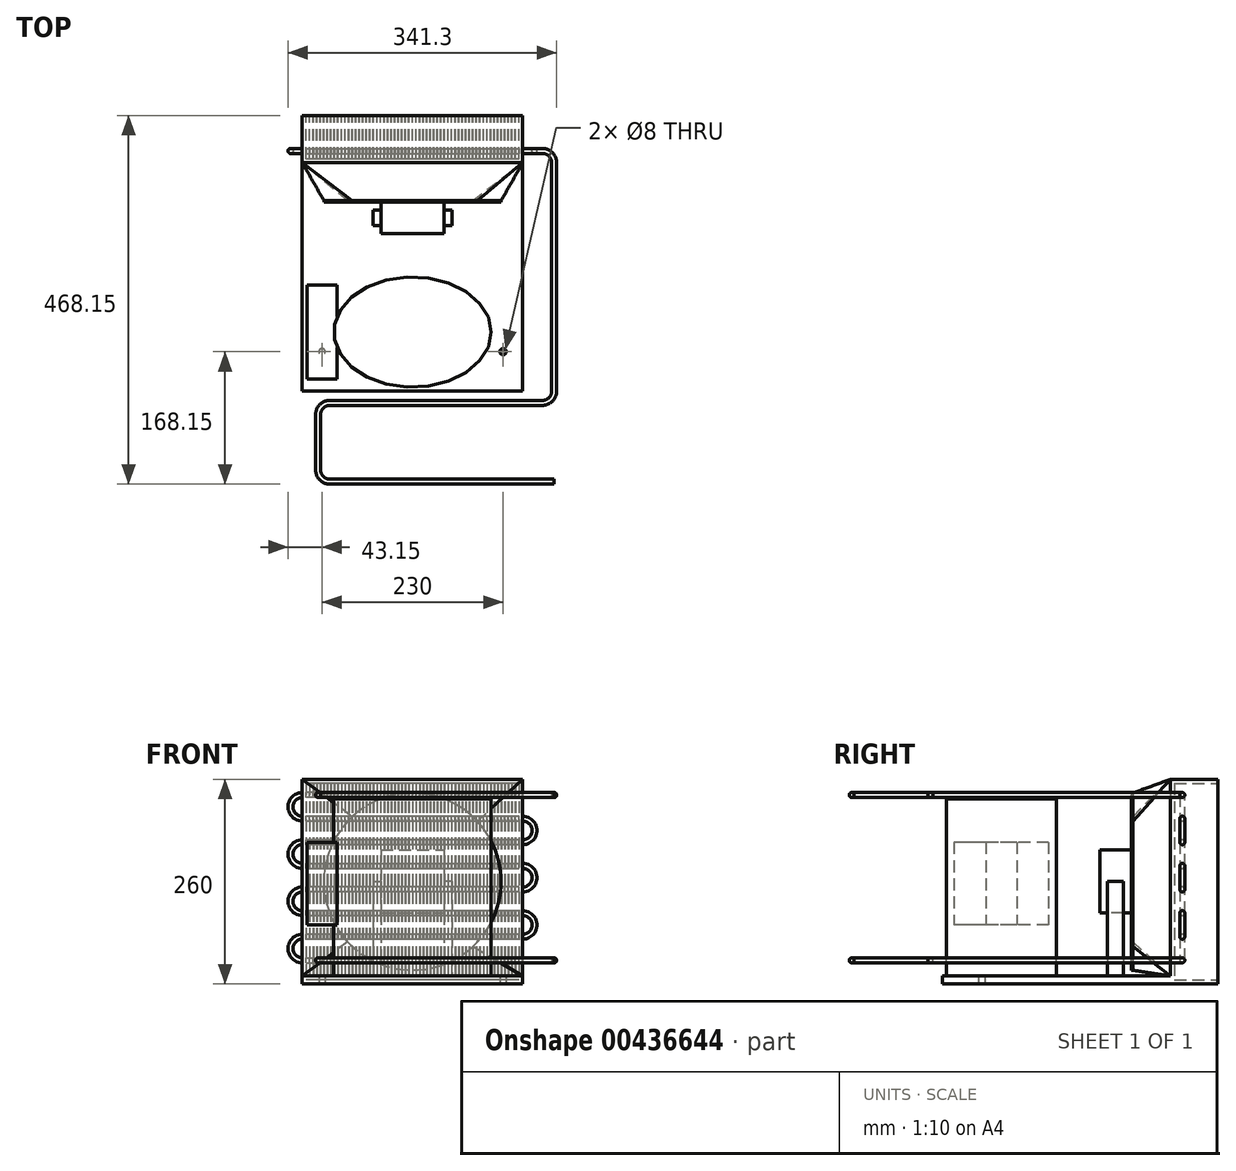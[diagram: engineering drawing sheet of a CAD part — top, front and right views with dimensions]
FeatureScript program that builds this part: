
annotation { "Feature Type Name" : "Feature", "Feature Type Description" : "" }
export const myFeature = defineFeature(function(context is Context, id is Id, definition is map)
    precondition{}
    {
        {
            var Q0;
            Q0=qCreatedBy(makeId("Top.planeOp"),FACE);
            var sketch = newSketch(context, id + "F0", { "sketchPlane" : qUnion([Q0])});
            skLineSegment(sketch, "E0", {"start": v(0, 0) * mm, "end": v(280, 0) * mm});
            skLineSegment(sketch, "E1", {"start": v(280, -350) * mm, "end": v(0, -350) * mm});
            skLineSegment(sketch, "E2", {"start": v(0, -350) * mm, "end": v(0, 0) * mm});
            skLineSegment(sketch, "E3", {"start": v(280, 0) * mm, "end": v(280, -60) * mm});
            skLineSegment(sketch, "E4", {"start": v(280, -60) * mm, "end": v(0, -60) * mm});
            skLineSegment(sketch, "E5", {"start": v(280, -350) * mm, "end": v(280, -200) * mm});
            skLineSegment(sketch, "E6", {"start": v(280, -200) * mm, "end": v(280, -60) * mm});
            skLineSegment(sketch, "E7", {"start": v(280, -275) * mm, "end": v(140, -275) * mm, "construction": true});
            skPoint(sketch, "E7.endSnap0", {"position": v(280, -275) * mm});
            skEllipse(sketch, "E8", {"center": v(140, -275) * mm, "majorRadius": 100 * mm, "minorRadius": 70 * mm, "majorAxis": v(1, 0)});
            skPoint(sketch, "E9.endSnap0", {"position": v(40, -275) * mm});
            skLineSegment(sketch, "E10.bottom", {"start": v(44, -215) * mm, "end": v(6, -215) * mm});
            skLineSegment(sketch, "E10.top", {"start": v(44, -335) * mm, "end": v(6, -335) * mm});
            skLineSegment(sketch, "E10.left", {"start": v(44, -215) * mm, "end": v(44, -335) * mm});
            skLineSegment(sketch, "E10.right", {"start": v(6, -215) * mm, "end": v(6, -335) * mm});
            skLineSegment(sketch, "E11", {"start": v(140, -60) * mm, "end": v(140, -110) * mm, "construction": true});
            skLineSegment(sketch, "E12", {"start": v(140, -110) * mm, "end": v(100, -110) * mm, "construction": true});
            skLineSegment(sketch, "E13.bottom", {"start": v(100, -110) * mm, "end": v(180, -110) * mm});
            skLineSegment(sketch, "E13.top", {"start": v(100, -150) * mm, "end": v(180, -150) * mm});
            skLineSegment(sketch, "E13.right", {"start": v(180, -110) * mm, "end": v(180, -150) * mm});
            skLineSegment(sketch, "E14.top", {"start": v(90, -140) * mm, "end": v(100, -140) * mm});
            skLineSegment(sketch, "E15.top", {"start": v(90, -120) * mm, "end": v(100, -120) * mm});
            skLineSegment(sketch, "E16", {"start": v(90, -120) * mm, "end": v(90, -140) * mm});
            skLineSegment(sketch, "E17", {"start": v(100, -150) * mm, "end": v(100, -110) * mm});
            skLineSegment(sketch, "E18", {"start": v(180, -140) * mm, "end": v(190, -140) * mm});
            skLineSegment(sketch, "E19", {"start": v(190, -140) * mm, "end": v(190, -120) * mm});
            skLineSegment(sketch, "E20", {"start": v(190, -120) * mm, "end": v(180, -120) * mm});
            skLineSegment(sketch, "E21", {"start": v(140, -275) * mm, "end": v(6, -275) * mm, "construction": true});
            skLineSegment(sketch, "E22", {"start": v(280, -350) * mm, "end": v(280, -300) * mm});
            skLineSegment(sketch, "E23", {"start": v(280, -300) * mm, "end": v(255, -300) * mm, "construction": true});
            skCircle(sketch, "E24", {"center": v(255, -300) * mm, "radius": 4 * mm});
            skLineSegment(sketch, "E25", {"start": v(255, -300) * mm, "end": v(25, -300) * mm, "construction": true});
            skCircle(sketch, "E26", {"center": v(25, -300) * mm, "radius": 4 * mm});
            skSolve(sketch);
        }
        {
            var Q0;
            {var subQ5=sQuery(id+"F0.wireOp",EDGE,"E1");Q0=makeQuery(id+"F0.imprint","IMPRINT",FACE,{"disambiguationData":[TD([[makeQuery(id+"F0.imprint","IMPRINT",EDGE,{"derivedFrom":subQ5}),-1.0]])]});}
            var Q1;
            Q1=makeQuery(id+"F0.imprint","IMPRINT",FACE,{"disambiguationData":[TD([[makeQuery(id+"F0.imprint","IMPRINT",EDGE,{"derivedFrom":sQuery(id+"F0.wireOp",EDGE,"E10.bottom")}),1.0]])]});
            var Q2;
            {var subQ3=sQuery(id+"F0.wireOp",EDGE,"E13.bottom");Q2=makeQuery(id+"F0.imprint","IMPRINT",FACE,{"disambiguationData":[TD([[makeQuery(id+"F0.imprint","IMPRINT",EDGE,{"derivedFrom":subQ3}),-1.0]])]});}
            extrude(context, id + "F1", {"entities" : qUnion([Q0, Q1, Q2]), "depth" : 10 * mm});
        }
        {
            var Q0;
            {var subQ0=sQuery(id+"F0.wireOp",EDGE,"E0");Q0=makeQuery(id+"F0.imprint","IMPRINT",FACE,{"disambiguationData":[TD([[makeQuery(id+"F0.imprint","IMPRINT",EDGE,{"derivedFrom":subQ0}),-1.0]])]});}
            extrude(context, id + "F2", {"entities" : qUnion([Q0]), "operationType" : NewBodyOperationType.ADD, "depth" : 260 * mm});
        }
        {
            var Q0;
            Q0=makeQuery(id+"F0.imprint","IMPRINT",FACE,{"disambiguationData":[TD([[makeQuery(id+"F0.imprint","IMPRINT",EDGE,{"derivedFrom":sQuery(id+"F0.wireOp",EDGE,"E8")}),1.0]])]});
            extrude(context, id + "F3", {"entities" : qUnion([Q0]), "operationType" : NewBodyOperationType.ADD, "depth" : 235 * mm});
        }
        {
            var Q0;
            Q0=makeQuery(id+"F0.imprint","IMPRINT",FACE,{"disambiguationData":[TD([[makeQuery(id+"F0.imprint","IMPRINT",EDGE,{"derivedFrom":sQuery(id+"F0.wireOp",EDGE,"E10.bottom")}),1.0]])]});
            var Q1;
            Q1=makeQuery(id+"F0.imprint","IMPRINT",FACE,{"disambiguationData":[TD([[makeQuery(id+"F0.imprint","IMPRINT",EDGE,{"derivedFrom":sQuery(id+"F0.wireOp",EDGE,"E26")}),1.0]])]});
            extrude(context, id + "F4", {"entities" : qUnion([Q0, Q1]), "operationType" : NewBodyOperationType.ADD, "depth" : 180 * mm, "hasSecondDirection" : true, "secondDirectionOppositeDirection" : false, "secondDirectionDepth" : 75 * mm});
        }
        {
            var Q0;
            {var subQ0=sQuery(id+"F0.wireOp",EDGE,"E14.top");Q0=makeQuery(id+"F0.imprint","IMPRINT",FACE,{"disambiguationData":[TD([[makeQuery(id+"F0.imprint","IMPRINT",EDGE,{"derivedFrom":subQ0}),1.0]])]});}
            var Q1;
            {var subQ0=sQuery(id+"F0.wireOp",EDGE,"E18");Q1=makeQuery(id+"F0.imprint","IMPRINT",FACE,{"disambiguationData":[TD([[makeQuery(id+"F0.imprint","IMPRINT",EDGE,{"derivedFrom":subQ0}),1.0]])]});}
            extrude(context, id + "F5", {"entities" : qUnion([Q0, Q1]), "operationType" : NewBodyOperationType.ADD, "depth" : 130 * mm});
        }
        {
            var Q0;
            {var subQ3=sQuery(id+"F0.wireOp",EDGE,"E13.bottom");Q0=makeQuery(id+"F0.imprint","IMPRINT",FACE,{"disambiguationData":[TD([[makeQuery(id+"F0.imprint","IMPRINT",EDGE,{"derivedFrom":subQ3}),-1.0]])]});}
            extrude(context, id + "F6", {"entities" : qUnion([Q0]), "operationType" : NewBodyOperationType.ADD, "depth" : 170 * mm, "hasSecondDirection" : true, "secondDirectionOppositeDirection" : false, "secondDirectionDepth" : 90 * mm});
        }
        {
            var Q0;
            Q0=makeQuery(id+"F6.opExtrude","SWEPT_FACE",FACE,{"disambiguationData":[OSD([sQuery(id+"F0.wireOp",EDGE,"E13.bottom")])]});
            var sketch = newSketch(context, id + "F7", { "sketchPlane" : qUnion([Q0])});
            skLineSegment(sketch, "E27", {"start": v(-140, 170) * mm, "end": v(-140, 90) * mm, "construction": true});
            skCircle(sketch, "E28", {"center": v(-140, 130) * mm, "radius": 112.5 * mm});
            skSolve(sketch);
        }
        {
            var Q0;
            Q0=makeQuery(id+"F7.imprint","IMPRINT",FACE,{"disambiguationData":[TD([[makeQuery(id+"F7.imprint","IMPRINT",EDGE,{"derivedFrom":sQuery(id+"F7.wireOp",EDGE,"E28")}),1.0]])]});
            var Q1;
            {var subQ0=sQuery(id+"F0.wireOp",EDGE,"E13.bottom");Q1=makeQuery(id+"F7.imprint","IMPRINT",FACE,{"disambiguationData":[TD([[makeQuery(id+"F7.imprint","IMPRINT",EDGE,{"derivedFrom":makeQuery(id+"F6.opExtrude","CAP_EDGE",EDGE,{"disambiguationData":[OSD([subQ0])],"isStart":true})}),-1.0]])]});}
            extrude(context, id + "F8", {"entities" : qUnion([Q0, Q1]), "operationType" : NewBodyOperationType.ADD, "depth" : 2 * mm});
        }
        {
            var Q1;
            Q1=makeQuery(id+"F8.opExtrude","CAP_FACE",FACE,{"disambiguationData":[OSD([sQuery(id+"F7.wireOp",EDGE,"E28")])],"isStart":false});
            var Q2;
            Q2=makeQuery(id+"F2.opExtrude","SWEPT_FACE",FACE,{"disambiguationData":[OSD([sQuery(id+"F0.wireOp",EDGE,"E4")])]});
            loft(context, id + "F9", {"operationType" : NewBodyOperationType.ADD, "sheetProfilesArray" : [{ "sheetProfileEntities" : qUnion([Q1]) }, { "sheetProfileEntities" : qUnion([Q2]) }]});
        }
        {
            var Q0;
            Q0=makeQuery(id+"F2.boolean.opBoolean","MERGE",FACE,{"derivedFrom":[makeQuery(id+"F1.opExtrude","SWEPT_FACE",FACE,{"disambiguationData":[OSD([sQuery(id+"F0.wireOp",EDGE,"E5"),sQuery(id+"F0.wireOp",EDGE,"E6")])]}),makeQuery(id+"F2.opExtrude","SWEPT_FACE",FACE,{"disambiguationData":[OSD([sQuery(id+"F0.wireOp",EDGE,"E3")])]})]});
            var sketch = newSketch(context, id + "F10", { "sketchPlane" : qUnion([Q0])});
            skLineSegment(sketch, "E29", {"start": v(-30, 260) * mm, "end": v(-30, 240) * mm, "construction": true});
            skLineSegment(sketch, "E30", {"start": v(-30, 240) * mm, "end": v(-45, 240) * mm, "construction": true});
            skCircle(sketch, "E31", {"center": v(-45, 240) * mm, "radius": 3.15 * mm});
            skLineSegment(sketch, "E32", {"start": v(-45, 240) * mm, "end": v(-45, 30) * mm, "construction": true});
            skCircle(sketch, "E33", {"center": v(-45, 30) * mm, "radius": 3.15 * mm});
            skSolve(sketch);
        }
        {
            var Q0;
            Q0=makeQuery(id+"F2.opExtrude","CAP_FACE",FACE,{"disambiguationData":[OSD([sQuery(id+"F0.wireOp",EDGE,"E0"),sQuery(id+"F0.wireOp",EDGE,"E2"),sQuery(id+"F0.wireOp",EDGE,"E3"),sQuery(id+"F0.wireOp",EDGE,"E4")])],"isStart":false});
            var sketch = newSketch(context, id + "F11", { "sketchPlane" : qUnion([Q0])});
            skLineSegment(sketch, "E34", {"start": v(280, -30) * mm, "end": v(280, -45) * mm, "construction": true});
            skLineSegment(sketch, "E35", {"start": v(280, -45) * mm, "end": v(305, -45) * mm});
            skLineSegment(sketch, "E36", {"start": v(320, -60) * mm, "end": v(320, -350) * mm});
            skPoint(sketch, "E37.visualSharp", {"position": v(320, -45) * mm});
            skArc(sketch, "E37.filletArc", {"start": v(320, -60) * mm, "mid": v(315.6, -49.4) * mm, "end": v(305, -45) * mm});
            skLineSegment(sketch, "E38", {"start": v(305, -365) * mm, "end": v(35, -365) * mm});
            skPoint(sketch, "E39.visualSharp", {"position": v(320, -365) * mm});
            skArc(sketch, "E39.filletArc", {"start": v(305, -365) * mm, "mid": v(315.6, -360.6) * mm, "end": v(320, -350) * mm});
            skLineSegment(sketch, "E40", {"start": v(20, -380) * mm, "end": v(20, -450) * mm});
            skLineSegment(sketch, "E41", {"start": v(35, -465) * mm, "end": v(320, -465) * mm});
            skPoint(sketch, "E42.visualSharp", {"position": v(20, -365) * mm});
            skArc(sketch, "E42.filletArc", {"start": v(35, -365) * mm, "mid": v(24.4, -369.4) * mm, "end": v(20, -380) * mm});
            skPoint(sketch, "E43.visualSharp", {"position": v(20, -465) * mm});
            skArc(sketch, "E43.filletArc", {"start": v(20, -450) * mm, "mid": v(24.4, -460.6) * mm, "end": v(35, -465) * mm});
            skSolve(sketch);
        }
        {
            var Q0;
            Q0=makeQuery(id+"F10.imprint","IMPRINT",FACE,{"disambiguationData":[TD([[makeQuery(id+"F10.imprint","IMPRINT",EDGE,{"derivedFrom":sQuery(id+"F10.wireOp",EDGE,"E31")}),1.0]])]});
            var Q1;
            Q1=makeQuery(id+"F10.imprint","IMPRINT",FACE,{"disambiguationData":[TD([[makeQuery(id+"F10.imprint","IMPRINT",EDGE,{"derivedFrom":sQuery(id+"F10.wireOp",EDGE,"E33")}),1.0]])]});
            var Q2;
            Q2=sQuery(id+"F11.wireOp",EDGE,"E35");
            var Q3;
            Q3=sQuery(id+"F11.wireOp",EDGE,"E37.filletArc");
            var Q4;
            Q4=sQuery(id+"F11.wireOp",EDGE,"E36");
            var Q5;
            Q5=sQuery(id+"F11.wireOp",EDGE,"E39.filletArc");
            var Q6;
            Q6=sQuery(id+"F11.wireOp",EDGE,"E38");
            var Q7;
            Q7=sQuery(id+"F11.wireOp",EDGE,"E42.filletArc");
            var Q8;
            Q8=sQuery(id+"F11.wireOp",EDGE,"E40");
            var Q9;
            Q9=sQuery(id+"F11.wireOp",EDGE,"E43.filletArc");
            var Q10;
            Q10=sQuery(id+"F11.wireOp",EDGE,"E41");
            sweep(context, id + "F12", {"operationType" : NewBodyOperationType.ADD, "profiles" : qUnion([Q0, Q1]), "path" : qUnion([Q2, Q3, Q4, Q5, Q6, Q7, Q8, Q9, Q10])});
        }
        {
            var Q0;
            Q0=makeQuery(id+"F2.opExtrude","SWEPT_FACE",FACE,{"disambiguationData":[OSD([sQuery(id+"F0.wireOp",EDGE,"E0")])]});
            var sketch = newSketch(context, id + "F13", { "sketchPlane" : qUnion([Q0])});
            skLineSegment(sketch, "E44", {"start": v(-280, 260) * mm, "end": v(-275, 260) * mm, "construction": true});
            skLineSegment(sketch, "E45", {"start": v(-275, 260) * mm, "end": v(-275, 255) * mm, "construction": true});
            skLineSegment(sketch, "E46.bottom", {"start": v(-275, 255) * mm, "end": v(-271, 255) * mm});
            skLineSegment(sketch, "E46.top", {"start": v(-275, 5) * mm, "end": v(-271, 5) * mm});
            skLineSegment(sketch, "E46.left", {"start": v(-275, 255) * mm, "end": v(-275, 5) * mm});
            skLineSegment(sketch, "E46.right", {"start": v(-271, 255) * mm, "end": v(-271, 5) * mm});
            skLineSegment(sketch, "E47.1.0.0", {"start": v(-266.5, 255) * mm, "end": v(-266.5, 5) * mm});
            skLineSegment(sketch, "E47.1.0.1", {"start": v(-270.5, 255) * mm, "end": v(-270.5, 5) * mm});
            skLineSegment(sketch, "E47.1.0.2", {"start": v(-270.5, 255) * mm, "end": v(-266.5, 255) * mm});
            skLineSegment(sketch, "E47.1.0.3", {"start": v(-270.5, 5) * mm, "end": v(-266.5, 5) * mm});
            skLineSegment(sketch, "E47.2.0.0", {"start": v(-261.98, 255) * mm, "end": v(-261.98, 5) * mm});
            skLineSegment(sketch, "E47.2.0.1", {"start": v(-265.98, 255) * mm, "end": v(-265.98, 5) * mm});
            skLineSegment(sketch, "E47.2.0.2", {"start": v(-265.98, 255) * mm, "end": v(-261.98, 255) * mm});
            skLineSegment(sketch, "E47.2.0.3", {"start": v(-265.98, 5) * mm, "end": v(-261.98, 5) * mm});
            skLineSegment(sketch, "E47.3.0.0", {"start": v(-257.47, 255) * mm, "end": v(-257.47, 5) * mm});
            skLineSegment(sketch, "E47.3.0.1", {"start": v(-261.47, 255) * mm, "end": v(-261.47, 5) * mm});
            skLineSegment(sketch, "E47.3.0.2", {"start": v(-261.47, 255) * mm, "end": v(-257.47, 255) * mm});
            skLineSegment(sketch, "E47.3.0.3", {"start": v(-261.47, 5) * mm, "end": v(-257.47, 5) * mm});
            skLineSegment(sketch, "E47.4.0.0", {"start": v(-252.97, 255) * mm, "end": v(-252.97, 5) * mm});
            skLineSegment(sketch, "E47.4.0.1", {"start": v(-256.97, 255) * mm, "end": v(-256.97, 5) * mm});
            skLineSegment(sketch, "E47.4.0.2", {"start": v(-256.97, 255) * mm, "end": v(-252.97, 255) * mm});
            skLineSegment(sketch, "E47.4.0.3", {"start": v(-256.97, 5) * mm, "end": v(-252.97, 5) * mm});
            skLineSegment(sketch, "E47.5.0.0", {"start": v(-248.46, 255) * mm, "end": v(-248.46, 5) * mm});
            skLineSegment(sketch, "E47.5.0.1", {"start": v(-252.46, 255) * mm, "end": v(-252.46, 5) * mm});
            skLineSegment(sketch, "E47.5.0.2", {"start": v(-252.46, 255) * mm, "end": v(-248.46, 255) * mm});
            skLineSegment(sketch, "E47.5.0.3", {"start": v(-252.46, 5) * mm, "end": v(-248.46, 5) * mm});
            skLineSegment(sketch, "E47.6.0.0", {"start": v(-243.95, 255) * mm, "end": v(-243.95, 5) * mm});
            skLineSegment(sketch, "E47.6.0.1", {"start": v(-247.95, 255) * mm, "end": v(-247.95, 5) * mm});
            skLineSegment(sketch, "E47.6.0.2", {"start": v(-247.95, 255) * mm, "end": v(-243.95, 255) * mm});
            skLineSegment(sketch, "E47.6.0.3", {"start": v(-247.95, 5) * mm, "end": v(-243.95, 5) * mm});
            skLineSegment(sketch, "E47.7.0.0", {"start": v(-239.44, 255) * mm, "end": v(-239.44, 5) * mm});
            skLineSegment(sketch, "E47.7.0.1", {"start": v(-243.44, 255) * mm, "end": v(-243.44, 5) * mm});
            skLineSegment(sketch, "E47.7.0.2", {"start": v(-243.44, 255) * mm, "end": v(-239.44, 255) * mm});
            skLineSegment(sketch, "E47.7.0.3", {"start": v(-243.44, 5) * mm, "end": v(-239.44, 5) * mm});
            skLineSegment(sketch, "E47.8.0.0", {"start": v(-234.93, 255) * mm, "end": v(-234.93, 5) * mm});
            skLineSegment(sketch, "E47.8.0.1", {"start": v(-238.93, 255) * mm, "end": v(-238.93, 5) * mm});
            skLineSegment(sketch, "E47.8.0.2", {"start": v(-238.93, 255) * mm, "end": v(-234.93, 255) * mm});
            skLineSegment(sketch, "E47.8.0.3", {"start": v(-238.93, 5) * mm, "end": v(-234.93, 5) * mm});
            skLineSegment(sketch, "E47.9.0.0", {"start": v(-230.42, 255) * mm, "end": v(-230.42, 5) * mm});
            skLineSegment(sketch, "E47.9.0.1", {"start": v(-234.42, 255) * mm, "end": v(-234.42, 5) * mm});
            skLineSegment(sketch, "E47.9.0.2", {"start": v(-234.42, 255) * mm, "end": v(-230.42, 255) * mm});
            skLineSegment(sketch, "E47.9.0.3", {"start": v(-234.42, 5) * mm, "end": v(-230.42, 5) * mm});
            skLineSegment(sketch, "E47.10.0.0", {"start": v(-225.92, 255) * mm, "end": v(-225.92, 5) * mm});
            skLineSegment(sketch, "E47.10.0.1", {"start": v(-229.92, 255) * mm, "end": v(-229.92, 5) * mm});
            skLineSegment(sketch, "E47.10.0.2", {"start": v(-229.92, 255) * mm, "end": v(-225.92, 255) * mm});
            skLineSegment(sketch, "E47.10.0.3", {"start": v(-229.92, 5) * mm, "end": v(-225.92, 5) * mm});
            skLineSegment(sketch, "E47.11.0.0", {"start": v(-221.4, 255) * mm, "end": v(-221.4, 5) * mm});
            skLineSegment(sketch, "E47.11.0.1", {"start": v(-225.4, 255) * mm, "end": v(-225.4, 5) * mm});
            skLineSegment(sketch, "E47.11.0.2", {"start": v(-225.4, 255) * mm, "end": v(-221.4, 255) * mm});
            skLineSegment(sketch, "E47.11.0.3", {"start": v(-225.4, 5) * mm, "end": v(-221.4, 5) * mm});
            skLineSegment(sketch, "E47.12.0.0", {"start": v(-216.9, 255) * mm, "end": v(-216.9, 5) * mm});
            skLineSegment(sketch, "E47.12.0.1", {"start": v(-220.9, 255) * mm, "end": v(-220.9, 5) * mm});
            skLineSegment(sketch, "E47.12.0.2", {"start": v(-220.9, 255) * mm, "end": v(-216.9, 255) * mm});
            skLineSegment(sketch, "E47.12.0.3", {"start": v(-220.9, 5) * mm, "end": v(-216.9, 5) * mm});
            skLineSegment(sketch, "E47.13.0.0", {"start": v(-212.39, 255) * mm, "end": v(-212.39, 5) * mm});
            skLineSegment(sketch, "E47.13.0.1", {"start": v(-216.39, 255) * mm, "end": v(-216.39, 5) * mm});
            skLineSegment(sketch, "E47.13.0.2", {"start": v(-216.39, 255) * mm, "end": v(-212.39, 255) * mm});
            skLineSegment(sketch, "E47.13.0.3", {"start": v(-216.39, 5) * mm, "end": v(-212.39, 5) * mm});
            skLineSegment(sketch, "E47.14.0.0", {"start": v(-207.88, 255) * mm, "end": v(-207.88, 5) * mm});
            skLineSegment(sketch, "E47.14.0.1", {"start": v(-211.88, 255) * mm, "end": v(-211.88, 5) * mm});
            skLineSegment(sketch, "E47.14.0.2", {"start": v(-211.88, 255) * mm, "end": v(-207.88, 255) * mm});
            skLineSegment(sketch, "E47.14.0.3", {"start": v(-211.88, 5) * mm, "end": v(-207.88, 5) * mm});
            skLineSegment(sketch, "E47.15.0.0", {"start": v(-203.37, 255) * mm, "end": v(-203.37, 5) * mm});
            skLineSegment(sketch, "E47.15.0.1", {"start": v(-207.37, 255) * mm, "end": v(-207.37, 5) * mm});
            skLineSegment(sketch, "E47.15.0.2", {"start": v(-207.37, 255) * mm, "end": v(-203.37, 255) * mm});
            skLineSegment(sketch, "E47.15.0.3", {"start": v(-207.37, 5) * mm, "end": v(-203.37, 5) * mm});
            skLineSegment(sketch, "E47.16.0.0", {"start": v(-198.86, 255) * mm, "end": v(-198.86, 5) * mm});
            skLineSegment(sketch, "E47.16.0.1", {"start": v(-202.86, 255) * mm, "end": v(-202.86, 5) * mm});
            skLineSegment(sketch, "E47.16.0.2", {"start": v(-202.86, 255) * mm, "end": v(-198.86, 255) * mm});
            skLineSegment(sketch, "E47.16.0.3", {"start": v(-202.86, 5) * mm, "end": v(-198.86, 5) * mm});
            skLineSegment(sketch, "E47.17.0.0", {"start": v(-194.36, 255) * mm, "end": v(-194.36, 5) * mm});
            skLineSegment(sketch, "E47.17.0.1", {"start": v(-198.36, 255) * mm, "end": v(-198.36, 5) * mm});
            skLineSegment(sketch, "E47.17.0.2", {"start": v(-198.36, 255) * mm, "end": v(-194.36, 255) * mm});
            skLineSegment(sketch, "E47.17.0.3", {"start": v(-198.36, 5) * mm, "end": v(-194.36, 5) * mm});
            skLineSegment(sketch, "E47.18.0.0", {"start": v(-189.85, 255) * mm, "end": v(-189.85, 5) * mm});
            skLineSegment(sketch, "E47.18.0.1", {"start": v(-193.85, 255) * mm, "end": v(-193.85, 5) * mm});
            skLineSegment(sketch, "E47.18.0.2", {"start": v(-193.85, 255) * mm, "end": v(-189.85, 255) * mm});
            skLineSegment(sketch, "E47.18.0.3", {"start": v(-193.85, 5) * mm, "end": v(-189.85, 5) * mm});
            skLineSegment(sketch, "E47.19.0.0", {"start": v(-185.34, 255) * mm, "end": v(-185.34, 5) * mm});
            skLineSegment(sketch, "E47.19.0.1", {"start": v(-189.34, 255) * mm, "end": v(-189.34, 5) * mm});
            skLineSegment(sketch, "E47.19.0.2", {"start": v(-189.34, 255) * mm, "end": v(-185.34, 255) * mm});
            skLineSegment(sketch, "E47.19.0.3", {"start": v(-189.34, 5) * mm, "end": v(-185.34, 5) * mm});
            skLineSegment(sketch, "E47.20.0.0", {"start": v(-180.83, 255) * mm, "end": v(-180.83, 5) * mm});
            skLineSegment(sketch, "E47.20.0.1", {"start": v(-184.83, 255) * mm, "end": v(-184.83, 5) * mm});
            skLineSegment(sketch, "E47.20.0.2", {"start": v(-184.83, 255) * mm, "end": v(-180.83, 255) * mm});
            skLineSegment(sketch, "E47.20.0.3", {"start": v(-184.83, 5) * mm, "end": v(-180.83, 5) * mm});
            skLineSegment(sketch, "E47.21.0.0", {"start": v(-176.32, 255) * mm, "end": v(-176.32, 5) * mm});
            skLineSegment(sketch, "E47.21.0.1", {"start": v(-180.32, 255) * mm, "end": v(-180.32, 5) * mm});
            skLineSegment(sketch, "E47.21.0.2", {"start": v(-180.32, 255) * mm, "end": v(-176.32, 255) * mm});
            skLineSegment(sketch, "E47.21.0.3", {"start": v(-180.32, 5) * mm, "end": v(-176.32, 5) * mm});
            skLineSegment(sketch, "E47.22.0.0", {"start": v(-171.81, 255) * mm, "end": v(-171.81, 5) * mm});
            skLineSegment(sketch, "E47.22.0.1", {"start": v(-175.81, 255) * mm, "end": v(-175.81, 5) * mm});
            skLineSegment(sketch, "E47.22.0.2", {"start": v(-175.81, 255) * mm, "end": v(-171.81, 255) * mm});
            skLineSegment(sketch, "E47.22.0.3", {"start": v(-175.81, 5) * mm, "end": v(-171.81, 5) * mm});
            skLineSegment(sketch, "E47.23.0.0", {"start": v(-167.3, 255) * mm, "end": v(-167.3, 5) * mm});
            skLineSegment(sketch, "E47.23.0.1", {"start": v(-171.3, 255) * mm, "end": v(-171.3, 5) * mm});
            skLineSegment(sketch, "E47.23.0.2", {"start": v(-171.3, 255) * mm, "end": v(-167.3, 255) * mm});
            skLineSegment(sketch, "E47.23.0.3", {"start": v(-171.3, 5) * mm, "end": v(-167.3, 5) * mm});
            skLineSegment(sketch, "E47.24.0.0", {"start": v(-162.8, 255) * mm, "end": v(-162.8, 5) * mm});
            skLineSegment(sketch, "E47.24.0.1", {"start": v(-166.8, 255) * mm, "end": v(-166.8, 5) * mm});
            skLineSegment(sketch, "E47.24.0.2", {"start": v(-166.8, 255) * mm, "end": v(-162.8, 255) * mm});
            skLineSegment(sketch, "E47.24.0.3", {"start": v(-166.8, 5) * mm, "end": v(-162.8, 5) * mm});
            skLineSegment(sketch, "E47.25.0.0", {"start": v(-158.29, 255) * mm, "end": v(-158.29, 5) * mm});
            skLineSegment(sketch, "E47.25.0.1", {"start": v(-162.29, 255) * mm, "end": v(-162.29, 5) * mm});
            skLineSegment(sketch, "E47.25.0.2", {"start": v(-162.29, 255) * mm, "end": v(-158.29, 255) * mm});
            skLineSegment(sketch, "E47.25.0.3", {"start": v(-162.29, 5) * mm, "end": v(-158.29, 5) * mm});
            skLineSegment(sketch, "E47.26.0.0", {"start": v(-153.78, 255) * mm, "end": v(-153.78, 5) * mm});
            skLineSegment(sketch, "E47.26.0.1", {"start": v(-157.78, 255) * mm, "end": v(-157.78, 5) * mm});
            skLineSegment(sketch, "E47.26.0.2", {"start": v(-157.78, 255) * mm, "end": v(-153.78, 255) * mm});
            skLineSegment(sketch, "E47.26.0.3", {"start": v(-157.78, 5) * mm, "end": v(-153.78, 5) * mm});
            skLineSegment(sketch, "E47.27.0.0", {"start": v(-149.27, 255) * mm, "end": v(-149.27, 5) * mm});
            skLineSegment(sketch, "E47.27.0.1", {"start": v(-153.27, 255) * mm, "end": v(-153.27, 5) * mm});
            skLineSegment(sketch, "E47.27.0.2", {"start": v(-153.27, 255) * mm, "end": v(-149.27, 255) * mm});
            skLineSegment(sketch, "E47.27.0.3", {"start": v(-153.27, 5) * mm, "end": v(-149.27, 5) * mm});
            skLineSegment(sketch, "E47.28.0.0", {"start": v(-144.76, 255) * mm, "end": v(-144.76, 5) * mm});
            skLineSegment(sketch, "E47.28.0.1", {"start": v(-148.76, 255) * mm, "end": v(-148.76, 5) * mm});
            skLineSegment(sketch, "E47.28.0.2", {"start": v(-148.76, 255) * mm, "end": v(-144.76, 255) * mm});
            skLineSegment(sketch, "E47.28.0.3", {"start": v(-148.76, 5) * mm, "end": v(-144.76, 5) * mm});
            skLineSegment(sketch, "E47.29.0.0", {"start": v(-140.25, 255) * mm, "end": v(-140.25, 5) * mm});
            skLineSegment(sketch, "E47.29.0.1", {"start": v(-144.25, 255) * mm, "end": v(-144.25, 5) * mm});
            skLineSegment(sketch, "E47.29.0.2", {"start": v(-144.25, 255) * mm, "end": v(-140.25, 255) * mm});
            skLineSegment(sketch, "E47.29.0.3", {"start": v(-144.25, 5) * mm, "end": v(-140.25, 5) * mm});
            skLineSegment(sketch, "E47.30.0.0", {"start": v(-135.75, 255) * mm, "end": v(-135.75, 5) * mm});
            skLineSegment(sketch, "E47.30.0.1", {"start": v(-139.75, 255) * mm, "end": v(-139.75, 5) * mm});
            skLineSegment(sketch, "E47.30.0.2", {"start": v(-139.75, 255) * mm, "end": v(-135.75, 255) * mm});
            skLineSegment(sketch, "E47.30.0.3", {"start": v(-139.75, 5) * mm, "end": v(-135.75, 5) * mm});
            skLineSegment(sketch, "E47.31.0.0", {"start": v(-131.24, 255) * mm, "end": v(-131.24, 5) * mm});
            skLineSegment(sketch, "E47.31.0.1", {"start": v(-135.24, 255) * mm, "end": v(-135.24, 5) * mm});
            skLineSegment(sketch, "E47.31.0.2", {"start": v(-135.24, 255) * mm, "end": v(-131.24, 255) * mm});
            skLineSegment(sketch, "E47.31.0.3", {"start": v(-135.24, 5) * mm, "end": v(-131.24, 5) * mm});
            skLineSegment(sketch, "E47.32.0.0", {"start": v(-126.73, 255) * mm, "end": v(-126.73, 5) * mm});
            skLineSegment(sketch, "E47.32.0.1", {"start": v(-130.73, 255) * mm, "end": v(-130.73, 5) * mm});
            skLineSegment(sketch, "E47.32.0.2", {"start": v(-130.73, 255) * mm, "end": v(-126.73, 255) * mm});
            skLineSegment(sketch, "E47.32.0.3", {"start": v(-130.73, 5) * mm, "end": v(-126.73, 5) * mm});
            skLineSegment(sketch, "E47.33.0.0", {"start": v(-122.22, 255) * mm, "end": v(-122.22, 5) * mm});
            skLineSegment(sketch, "E47.33.0.1", {"start": v(-126.22, 255) * mm, "end": v(-126.22, 5) * mm});
            skLineSegment(sketch, "E47.33.0.2", {"start": v(-126.22, 255) * mm, "end": v(-122.22, 255) * mm});
            skLineSegment(sketch, "E47.33.0.3", {"start": v(-126.22, 5) * mm, "end": v(-122.22, 5) * mm});
            skLineSegment(sketch, "E47.34.0.0", {"start": v(-117.71, 255) * mm, "end": v(-117.71, 5) * mm});
            skLineSegment(sketch, "E47.34.0.1", {"start": v(-121.71, 255) * mm, "end": v(-121.71, 5) * mm});
            skLineSegment(sketch, "E47.34.0.2", {"start": v(-121.71, 255) * mm, "end": v(-117.71, 255) * mm});
            skLineSegment(sketch, "E47.34.0.3", {"start": v(-121.71, 5) * mm, "end": v(-117.71, 5) * mm});
            skLineSegment(sketch, "E47.35.0.0", {"start": v(-113.2, 255) * mm, "end": v(-113.2, 5) * mm});
            skLineSegment(sketch, "E47.35.0.1", {"start": v(-117.2, 255) * mm, "end": v(-117.2, 5) * mm});
            skLineSegment(sketch, "E47.35.0.2", {"start": v(-117.2, 255) * mm, "end": v(-113.2, 255) * mm});
            skLineSegment(sketch, "E47.35.0.3", {"start": v(-117.2, 5) * mm, "end": v(-113.2, 5) * mm});
            skLineSegment(sketch, "E47.36.0.0", {"start": v(-108.7, 255) * mm, "end": v(-108.7, 5) * mm});
            skLineSegment(sketch, "E47.36.0.1", {"start": v(-112.7, 255) * mm, "end": v(-112.7, 5) * mm});
            skLineSegment(sketch, "E47.36.0.2", {"start": v(-112.7, 255) * mm, "end": v(-108.7, 255) * mm});
            skLineSegment(sketch, "E47.36.0.3", {"start": v(-112.7, 5) * mm, "end": v(-108.7, 5) * mm});
            skLineSegment(sketch, "E47.37.0.0", {"start": v(-104.19, 255) * mm, "end": v(-104.19, 5) * mm});
            skLineSegment(sketch, "E47.37.0.1", {"start": v(-108.19, 255) * mm, "end": v(-108.19, 5) * mm});
            skLineSegment(sketch, "E47.37.0.2", {"start": v(-108.19, 255) * mm, "end": v(-104.19, 255) * mm});
            skLineSegment(sketch, "E47.37.0.3", {"start": v(-108.19, 5) * mm, "end": v(-104.19, 5) * mm});
            skLineSegment(sketch, "E47.38.0.0", {"start": v(-99.68, 255) * mm, "end": v(-99.68, 5) * mm});
            skLineSegment(sketch, "E47.38.0.1", {"start": v(-103.68, 255) * mm, "end": v(-103.68, 5) * mm});
            skLineSegment(sketch, "E47.38.0.2", {"start": v(-103.68, 255) * mm, "end": v(-99.68, 255) * mm});
            skLineSegment(sketch, "E47.38.0.3", {"start": v(-103.68, 5) * mm, "end": v(-99.68, 5) * mm});
            skLineSegment(sketch, "E47.39.0.0", {"start": v(-95.17, 255) * mm, "end": v(-95.17, 5) * mm});
            skLineSegment(sketch, "E47.39.0.1", {"start": v(-99.17, 255) * mm, "end": v(-99.17, 5) * mm});
            skLineSegment(sketch, "E47.39.0.2", {"start": v(-99.17, 255) * mm, "end": v(-95.17, 255) * mm});
            skLineSegment(sketch, "E47.39.0.3", {"start": v(-99.17, 5) * mm, "end": v(-95.17, 5) * mm});
            skLineSegment(sketch, "E47.40.0.0", {"start": v(-90.66, 255) * mm, "end": v(-90.66, 5) * mm});
            skLineSegment(sketch, "E47.40.0.1", {"start": v(-94.66, 255) * mm, "end": v(-94.66, 5) * mm});
            skLineSegment(sketch, "E47.40.0.2", {"start": v(-94.66, 255) * mm, "end": v(-90.66, 255) * mm});
            skLineSegment(sketch, "E47.40.0.3", {"start": v(-94.66, 5) * mm, "end": v(-90.66, 5) * mm});
            skLineSegment(sketch, "E47.41.0.0", {"start": v(-86.15, 255) * mm, "end": v(-86.15, 5) * mm});
            skLineSegment(sketch, "E47.41.0.1", {"start": v(-90.15, 255) * mm, "end": v(-90.15, 5) * mm});
            skLineSegment(sketch, "E47.41.0.2", {"start": v(-90.15, 255) * mm, "end": v(-86.15, 255) * mm});
            skLineSegment(sketch, "E47.41.0.3", {"start": v(-90.15, 5) * mm, "end": v(-86.15, 5) * mm});
            skLineSegment(sketch, "E47.42.0.0", {"start": v(-81.64, 255) * mm, "end": v(-81.64, 5) * mm});
            skLineSegment(sketch, "E47.42.0.1", {"start": v(-85.64, 255) * mm, "end": v(-85.64, 5) * mm});
            skLineSegment(sketch, "E47.42.0.2", {"start": v(-85.64, 255) * mm, "end": v(-81.64, 255) * mm});
            skLineSegment(sketch, "E47.42.0.3", {"start": v(-85.64, 5) * mm, "end": v(-81.64, 5) * mm});
            skLineSegment(sketch, "E47.43.0.0", {"start": v(-77.14, 255) * mm, "end": v(-77.14, 5) * mm});
            skLineSegment(sketch, "E47.43.0.1", {"start": v(-81.14, 255) * mm, "end": v(-81.14, 5) * mm});
            skLineSegment(sketch, "E47.43.0.2", {"start": v(-81.14, 255) * mm, "end": v(-77.14, 255) * mm});
            skLineSegment(sketch, "E47.43.0.3", {"start": v(-81.14, 5) * mm, "end": v(-77.14, 5) * mm});
            skLineSegment(sketch, "E47.44.0.0", {"start": v(-72.63, 255) * mm, "end": v(-72.63, 5) * mm});
            skLineSegment(sketch, "E47.44.0.1", {"start": v(-76.63, 255) * mm, "end": v(-76.63, 5) * mm});
            skLineSegment(sketch, "E47.44.0.2", {"start": v(-76.63, 255) * mm, "end": v(-72.63, 255) * mm});
            skLineSegment(sketch, "E47.44.0.3", {"start": v(-76.63, 5) * mm, "end": v(-72.63, 5) * mm});
            skLineSegment(sketch, "E47.45.0.0", {"start": v(-68.12, 255) * mm, "end": v(-68.12, 5) * mm});
            skLineSegment(sketch, "E47.45.0.1", {"start": v(-72.12, 255) * mm, "end": v(-72.12, 5) * mm});
            skLineSegment(sketch, "E47.45.0.2", {"start": v(-72.12, 255) * mm, "end": v(-68.12, 255) * mm});
            skLineSegment(sketch, "E47.45.0.3", {"start": v(-72.12, 5) * mm, "end": v(-68.12, 5) * mm});
            skLineSegment(sketch, "E47.46.0.0", {"start": v(-63.61, 255) * mm, "end": v(-63.61, 5) * mm});
            skLineSegment(sketch, "E47.46.0.1", {"start": v(-67.61, 255) * mm, "end": v(-67.61, 5) * mm});
            skLineSegment(sketch, "E47.46.0.2", {"start": v(-67.61, 255) * mm, "end": v(-63.61, 255) * mm});
            skLineSegment(sketch, "E47.46.0.3", {"start": v(-67.61, 5) * mm, "end": v(-63.61, 5) * mm});
            skLineSegment(sketch, "E47.47.0.0", {"start": v(-59.1, 255) * mm, "end": v(-59.1, 5) * mm});
            skLineSegment(sketch, "E47.47.0.1", {"start": v(-63.1, 255) * mm, "end": v(-63.1, 5) * mm});
            skLineSegment(sketch, "E47.47.0.2", {"start": v(-63.1, 255) * mm, "end": v(-59.1, 255) * mm});
            skLineSegment(sketch, "E47.47.0.3", {"start": v(-63.1, 5) * mm, "end": v(-59.1, 5) * mm});
            skLineSegment(sketch, "E47.48.0.0", {"start": v(-54.6, 255) * mm, "end": v(-54.6, 5) * mm});
            skLineSegment(sketch, "E47.48.0.1", {"start": v(-58.6, 255) * mm, "end": v(-58.6, 5) * mm});
            skLineSegment(sketch, "E47.48.0.2", {"start": v(-58.6, 255) * mm, "end": v(-54.6, 255) * mm});
            skLineSegment(sketch, "E47.48.0.3", {"start": v(-58.6, 5) * mm, "end": v(-54.6, 5) * mm});
            skLineSegment(sketch, "E47.49.0.0", {"start": v(-50.08, 255) * mm, "end": v(-50.08, 5) * mm});
            skLineSegment(sketch, "E47.49.0.1", {"start": v(-54.08, 255) * mm, "end": v(-54.08, 5) * mm});
            skLineSegment(sketch, "E47.49.0.2", {"start": v(-54.08, 255) * mm, "end": v(-50.08, 255) * mm});
            skLineSegment(sketch, "E47.49.0.3", {"start": v(-54.08, 5) * mm, "end": v(-50.08, 5) * mm});
            skLineSegment(sketch, "E47.50.0.0", {"start": v(-45.58, 255) * mm, "end": v(-45.58, 5) * mm});
            skLineSegment(sketch, "E47.50.0.1", {"start": v(-49.58, 255) * mm, "end": v(-49.58, 5) * mm});
            skLineSegment(sketch, "E47.50.0.2", {"start": v(-49.58, 255) * mm, "end": v(-45.58, 255) * mm});
            skLineSegment(sketch, "E47.50.0.3", {"start": v(-49.58, 5) * mm, "end": v(-45.58, 5) * mm});
            skLineSegment(sketch, "E47.51.0.0", {"start": v(-41.07, 255) * mm, "end": v(-41.07, 5) * mm});
            skLineSegment(sketch, "E47.51.0.1", {"start": v(-45.07, 255) * mm, "end": v(-45.07, 5) * mm});
            skLineSegment(sketch, "E47.51.0.2", {"start": v(-45.07, 255) * mm, "end": v(-41.07, 255) * mm});
            skLineSegment(sketch, "E47.51.0.3", {"start": v(-45.07, 5) * mm, "end": v(-41.07, 5) * mm});
            skLineSegment(sketch, "E47.52.0.0", {"start": v(-36.56, 255) * mm, "end": v(-36.56, 5) * mm});
            skLineSegment(sketch, "E47.52.0.1", {"start": v(-40.56, 255) * mm, "end": v(-40.56, 5) * mm});
            skLineSegment(sketch, "E47.52.0.2", {"start": v(-40.56, 255) * mm, "end": v(-36.56, 255) * mm});
            skLineSegment(sketch, "E47.52.0.3", {"start": v(-40.56, 5) * mm, "end": v(-36.56, 5) * mm});
            skLineSegment(sketch, "E47.53.0.0", {"start": v(-32.05, 255) * mm, "end": v(-32.05, 5) * mm});
            skLineSegment(sketch, "E47.53.0.1", {"start": v(-36.05, 255) * mm, "end": v(-36.05, 5) * mm});
            skLineSegment(sketch, "E47.53.0.2", {"start": v(-36.05, 255) * mm, "end": v(-32.05, 255) * mm});
            skLineSegment(sketch, "E47.53.0.3", {"start": v(-36.05, 5) * mm, "end": v(-32.05, 5) * mm});
            skLineSegment(sketch, "E47.54.0.0", {"start": v(-27.54, 255) * mm, "end": v(-27.54, 5) * mm});
            skLineSegment(sketch, "E47.54.0.1", {"start": v(-31.54, 255) * mm, "end": v(-31.54, 5) * mm});
            skLineSegment(sketch, "E47.54.0.2", {"start": v(-31.54, 255) * mm, "end": v(-27.54, 255) * mm});
            skLineSegment(sketch, "E47.54.0.3", {"start": v(-31.54, 5) * mm, "end": v(-27.54, 5) * mm});
            skLineSegment(sketch, "E47.55.0.0", {"start": v(-23.03, 255) * mm, "end": v(-23.03, 5) * mm});
            skLineSegment(sketch, "E47.55.0.1", {"start": v(-27.03, 255) * mm, "end": v(-27.03, 5) * mm});
            skLineSegment(sketch, "E47.55.0.2", {"start": v(-27.03, 255) * mm, "end": v(-23.03, 255) * mm});
            skLineSegment(sketch, "E47.55.0.3", {"start": v(-27.03, 5) * mm, "end": v(-23.03, 5) * mm});
            skLineSegment(sketch, "E47.56.0.0", {"start": v(-18.53, 255) * mm, "end": v(-18.53, 5) * mm});
            skLineSegment(sketch, "E47.56.0.1", {"start": v(-22.53, 255) * mm, "end": v(-22.53, 5) * mm});
            skLineSegment(sketch, "E47.56.0.2", {"start": v(-22.53, 255) * mm, "end": v(-18.53, 255) * mm});
            skLineSegment(sketch, "E47.56.0.3", {"start": v(-22.53, 5) * mm, "end": v(-18.53, 5) * mm});
            skLineSegment(sketch, "E47.57.0.0", {"start": v(-14.02, 255) * mm, "end": v(-14.02, 5) * mm});
            skLineSegment(sketch, "E47.57.0.1", {"start": v(-18.02, 255) * mm, "end": v(-18.02, 5) * mm});
            skLineSegment(sketch, "E47.57.0.2", {"start": v(-18.02, 255) * mm, "end": v(-14.02, 255) * mm});
            skLineSegment(sketch, "E47.57.0.3", {"start": v(-18.02, 5) * mm, "end": v(-14.02, 5) * mm});
            skLineSegment(sketch, "E47.58.0.0", {"start": v(-9.5, 255) * mm, "end": v(-9.5, 5) * mm});
            skLineSegment(sketch, "E47.58.0.1", {"start": v(-13.5, 255) * mm, "end": v(-13.5, 5) * mm});
            skLineSegment(sketch, "E47.58.0.2", {"start": v(-13.5, 255) * mm, "end": v(-9.5, 255) * mm});
            skLineSegment(sketch, "E47.58.0.3", {"start": v(-13.5, 5) * mm, "end": v(-9.5, 5) * mm});
            skLineSegment(sketch, "E47.59.0.0", {"start": v(-5, 255) * mm, "end": v(-5, 5) * mm});
            skLineSegment(sketch, "E47.59.0.1", {"start": v(-9, 255) * mm, "end": v(-9, 5) * mm});
            skLineSegment(sketch, "E47.59.0.2", {"start": v(-9, 255) * mm, "end": v(-5, 255) * mm});
            skLineSegment(sketch, "E47.59.0.3", {"start": v(-9, 5) * mm, "end": v(-5, 5) * mm});
            skLineSegment(sketch, "E47.direction1", {"start": v(-271, 5) * mm, "end": v(-266.5, 5) * mm, "construction": true});
            skLineSegment(sketch, "E48.direction1", {"start": v(-275, 5) * mm, "end": v(-250, 5) * mm, "construction": true});
            skLineSegment(sketch, "E48.direction2", {"start": v(-275, 5) * mm, "end": v(-275, -8.22) * mm, "construction": true});
            skSolve(sketch);
        }
        {
            var Q0;
            Q0=makeQuery(id+"F13.imprint","IMPRINT",FACE,{"disambiguationData":[TD([[makeQuery(id+"F13.imprint","IMPRINT",EDGE,{"derivedFrom":sQuery(id+"F13.wireOp",EDGE,"E46.bottom")}),-1.0]])]});
            var Q1;
            Q1=makeQuery(id+"F13.imprint","IMPRINT",FACE,{"disambiguationData":[TD([[makeQuery(id+"F13.imprint","IMPRINT",EDGE,{"derivedFrom":sQuery(id+"F13.wireOp",EDGE,"E47.1.0.0")}),-1.0]])]});
            var Q2;
            Q2=makeQuery(id+"F13.imprint","IMPRINT",FACE,{"disambiguationData":[TD([[makeQuery(id+"F13.imprint","IMPRINT",EDGE,{"derivedFrom":sQuery(id+"F13.wireOp",EDGE,"E47.2.0.0")}),-1.0]])]});
            var Q3;
            Q3=makeQuery(id+"F13.imprint","IMPRINT",FACE,{"disambiguationData":[TD([[makeQuery(id+"F13.imprint","IMPRINT",EDGE,{"derivedFrom":sQuery(id+"F13.wireOp",EDGE,"E47.3.0.0")}),-1.0]])]});
            var Q4;
            Q4=makeQuery(id+"F13.imprint","IMPRINT",FACE,{"disambiguationData":[TD([[makeQuery(id+"F13.imprint","IMPRINT",EDGE,{"derivedFrom":sQuery(id+"F13.wireOp",EDGE,"E47.4.0.0")}),-1.0]])]});
            var Q5;
            Q5=makeQuery(id+"F13.imprint","IMPRINT",FACE,{"disambiguationData":[TD([[makeQuery(id+"F13.imprint","IMPRINT",EDGE,{"derivedFrom":sQuery(id+"F13.wireOp",EDGE,"E47.5.0.0")}),-1.0]])]});
            var Q6;
            Q6=makeQuery(id+"F13.imprint","IMPRINT",FACE,{"disambiguationData":[TD([[makeQuery(id+"F13.imprint","IMPRINT",EDGE,{"derivedFrom":sQuery(id+"F13.wireOp",EDGE,"E47.6.0.0")}),-1.0]])]});
            var Q7;
            Q7=makeQuery(id+"F13.imprint","IMPRINT",FACE,{"disambiguationData":[TD([[makeQuery(id+"F13.imprint","IMPRINT",EDGE,{"derivedFrom":sQuery(id+"F13.wireOp",EDGE,"E47.7.0.0")}),-1.0]])]});
            var Q8;
            Q8=makeQuery(id+"F13.imprint","IMPRINT",FACE,{"disambiguationData":[TD([[makeQuery(id+"F13.imprint","IMPRINT",EDGE,{"derivedFrom":sQuery(id+"F13.wireOp",EDGE,"E47.8.0.0")}),-1.0]])]});
            var Q9;
            Q9=makeQuery(id+"F13.imprint","IMPRINT",FACE,{"disambiguationData":[TD([[makeQuery(id+"F13.imprint","IMPRINT",EDGE,{"derivedFrom":sQuery(id+"F13.wireOp",EDGE,"E47.9.0.0")}),-1.0]])]});
            var Q10;
            Q10=makeQuery(id+"F13.imprint","IMPRINT",FACE,{"disambiguationData":[TD([[makeQuery(id+"F13.imprint","IMPRINT",EDGE,{"derivedFrom":sQuery(id+"F13.wireOp",EDGE,"E47.10.0.0")}),-1.0]])]});
            var Q11;
            Q11=makeQuery(id+"F13.imprint","IMPRINT",FACE,{"disambiguationData":[TD([[makeQuery(id+"F13.imprint","IMPRINT",EDGE,{"derivedFrom":sQuery(id+"F13.wireOp",EDGE,"E47.11.0.0")}),-1.0]])]});
            var Q12;
            Q12=makeQuery(id+"F13.imprint","IMPRINT",FACE,{"disambiguationData":[TD([[makeQuery(id+"F13.imprint","IMPRINT",EDGE,{"derivedFrom":sQuery(id+"F13.wireOp",EDGE,"E47.14.0.0")}),-1.0]])]});
            var Q13;
            Q13=makeQuery(id+"F13.imprint","IMPRINT",FACE,{"disambiguationData":[TD([[makeQuery(id+"F13.imprint","IMPRINT",EDGE,{"derivedFrom":sQuery(id+"F13.wireOp",EDGE,"E47.17.0.0")}),-1.0]])]});
            var Q14;
            Q14=makeQuery(id+"F13.imprint","IMPRINT",FACE,{"disambiguationData":[TD([[makeQuery(id+"F13.imprint","IMPRINT",EDGE,{"derivedFrom":sQuery(id+"F13.wireOp",EDGE,"E47.20.0.0")}),-1.0]])]});
            var Q15;
            Q15=makeQuery(id+"F13.imprint","IMPRINT",FACE,{"disambiguationData":[TD([[makeQuery(id+"F13.imprint","IMPRINT",EDGE,{"derivedFrom":sQuery(id+"F13.wireOp",EDGE,"E47.23.0.0")}),-1.0]])]});
            var Q16;
            Q16=makeQuery(id+"F13.imprint","IMPRINT",FACE,{"disambiguationData":[TD([[makeQuery(id+"F13.imprint","IMPRINT",EDGE,{"derivedFrom":sQuery(id+"F13.wireOp",EDGE,"E47.25.0.0")}),-1.0]])]});
            var Q17;
            Q17=makeQuery(id+"F13.imprint","IMPRINT",FACE,{"disambiguationData":[TD([[makeQuery(id+"F13.imprint","IMPRINT",EDGE,{"derivedFrom":sQuery(id+"F13.wireOp",EDGE,"E47.27.0.0")}),-1.0]])]});
            var Q18;
            Q18=makeQuery(id+"F13.imprint","IMPRINT",FACE,{"disambiguationData":[TD([[makeQuery(id+"F13.imprint","IMPRINT",EDGE,{"derivedFrom":sQuery(id+"F13.wireOp",EDGE,"E47.29.0.0")}),-1.0]])]});
            var Q19;
            Q19=makeQuery(id+"F13.imprint","IMPRINT",FACE,{"disambiguationData":[TD([[makeQuery(id+"F13.imprint","IMPRINT",EDGE,{"derivedFrom":sQuery(id+"F13.wireOp",EDGE,"E47.32.0.0")}),-1.0]])]});
            var Q20;
            Q20=makeQuery(id+"F13.imprint","IMPRINT",FACE,{"disambiguationData":[TD([[makeQuery(id+"F13.imprint","IMPRINT",EDGE,{"derivedFrom":sQuery(id+"F13.wireOp",EDGE,"E47.37.0.0")}),-1.0]])]});
            var Q21;
            Q21=makeQuery(id+"F13.imprint","IMPRINT",FACE,{"disambiguationData":[TD([[makeQuery(id+"F13.imprint","IMPRINT",EDGE,{"derivedFrom":sQuery(id+"F13.wireOp",EDGE,"E47.40.0.0")}),-1.0]])]});
            var Q22;
            Q22=makeQuery(id+"F13.imprint","IMPRINT",FACE,{"disambiguationData":[TD([[makeQuery(id+"F13.imprint","IMPRINT",EDGE,{"derivedFrom":sQuery(id+"F13.wireOp",EDGE,"E47.41.0.0")}),-1.0]])]});
            var Q23;
            Q23=makeQuery(id+"F13.imprint","IMPRINT",FACE,{"disambiguationData":[TD([[makeQuery(id+"F13.imprint","IMPRINT",EDGE,{"derivedFrom":sQuery(id+"F13.wireOp",EDGE,"E47.44.0.0")}),-1.0]])]});
            var Q24;
            Q24=makeQuery(id+"F13.imprint","IMPRINT",FACE,{"disambiguationData":[TD([[makeQuery(id+"F13.imprint","IMPRINT",EDGE,{"derivedFrom":sQuery(id+"F13.wireOp",EDGE,"E47.47.0.0")}),-1.0]])]});
            var Q25;
            Q25=makeQuery(id+"F13.imprint","IMPRINT",FACE,{"disambiguationData":[TD([[makeQuery(id+"F13.imprint","IMPRINT",EDGE,{"derivedFrom":sQuery(id+"F13.wireOp",EDGE,"E47.50.0.0")}),-1.0]])]});
            var Q26;
            Q26=makeQuery(id+"F13.imprint","IMPRINT",FACE,{"disambiguationData":[TD([[makeQuery(id+"F13.imprint","IMPRINT",EDGE,{"derivedFrom":sQuery(id+"F13.wireOp",EDGE,"E47.52.0.0")}),-1.0]])]});
            var Q27;
            Q27=makeQuery(id+"F13.imprint","IMPRINT",FACE,{"disambiguationData":[TD([[makeQuery(id+"F13.imprint","IMPRINT",EDGE,{"derivedFrom":sQuery(id+"F13.wireOp",EDGE,"E47.55.0.0")}),-1.0]])]});
            var Q28;
            Q28=makeQuery(id+"F13.imprint","IMPRINT",FACE,{"disambiguationData":[TD([[makeQuery(id+"F13.imprint","IMPRINT",EDGE,{"derivedFrom":sQuery(id+"F13.wireOp",EDGE,"E47.12.0.0")}),-1.0]])]});
            var Q29;
            Q29=makeQuery(id+"F13.imprint","IMPRINT",FACE,{"disambiguationData":[TD([[makeQuery(id+"F13.imprint","IMPRINT",EDGE,{"derivedFrom":sQuery(id+"F13.wireOp",EDGE,"E47.13.0.0")}),-1.0]])]});
            var Q30;
            Q30=makeQuery(id+"F13.imprint","IMPRINT",FACE,{"disambiguationData":[TD([[makeQuery(id+"F13.imprint","IMPRINT",EDGE,{"derivedFrom":sQuery(id+"F13.wireOp",EDGE,"E47.15.0.0")}),-1.0]])]});
            var Q31;
            Q31=makeQuery(id+"F13.imprint","IMPRINT",FACE,{"disambiguationData":[TD([[makeQuery(id+"F13.imprint","IMPRINT",EDGE,{"derivedFrom":sQuery(id+"F13.wireOp",EDGE,"E47.16.0.0")}),-1.0]])]});
            var Q32;
            Q32=makeQuery(id+"F13.imprint","IMPRINT",FACE,{"disambiguationData":[TD([[makeQuery(id+"F13.imprint","IMPRINT",EDGE,{"derivedFrom":sQuery(id+"F13.wireOp",EDGE,"E47.18.0.0")}),-1.0]])]});
            var Q33;
            Q33=makeQuery(id+"F13.imprint","IMPRINT",FACE,{"disambiguationData":[TD([[makeQuery(id+"F13.imprint","IMPRINT",EDGE,{"derivedFrom":sQuery(id+"F13.wireOp",EDGE,"E47.19.0.0")}),-1.0]])]});
            var Q34;
            Q34=makeQuery(id+"F13.imprint","IMPRINT",FACE,{"disambiguationData":[TD([[makeQuery(id+"F13.imprint","IMPRINT",EDGE,{"derivedFrom":sQuery(id+"F13.wireOp",EDGE,"E47.21.0.0")}),-1.0]])]});
            var Q35;
            Q35=makeQuery(id+"F13.imprint","IMPRINT",FACE,{"disambiguationData":[TD([[makeQuery(id+"F13.imprint","IMPRINT",EDGE,{"derivedFrom":sQuery(id+"F13.wireOp",EDGE,"E47.22.0.0")}),-1.0]])]});
            var Q36;
            Q36=makeQuery(id+"F13.imprint","IMPRINT",FACE,{"disambiguationData":[TD([[makeQuery(id+"F13.imprint","IMPRINT",EDGE,{"derivedFrom":sQuery(id+"F13.wireOp",EDGE,"E47.24.0.0")}),-1.0]])]});
            var Q37;
            Q37=makeQuery(id+"F13.imprint","IMPRINT",FACE,{"disambiguationData":[TD([[makeQuery(id+"F13.imprint","IMPRINT",EDGE,{"derivedFrom":sQuery(id+"F13.wireOp",EDGE,"E47.26.0.0")}),-1.0]])]});
            var Q38;
            Q38=makeQuery(id+"F13.imprint","IMPRINT",FACE,{"disambiguationData":[TD([[makeQuery(id+"F13.imprint","IMPRINT",EDGE,{"derivedFrom":sQuery(id+"F13.wireOp",EDGE,"E47.28.0.0")}),-1.0]])]});
            var Q39;
            Q39=makeQuery(id+"F13.imprint","IMPRINT",FACE,{"disambiguationData":[TD([[makeQuery(id+"F13.imprint","IMPRINT",EDGE,{"derivedFrom":sQuery(id+"F13.wireOp",EDGE,"E47.30.0.0")}),-1.0]])]});
            var Q40;
            Q40=makeQuery(id+"F13.imprint","IMPRINT",FACE,{"disambiguationData":[TD([[makeQuery(id+"F13.imprint","IMPRINT",EDGE,{"derivedFrom":sQuery(id+"F13.wireOp",EDGE,"E47.31.0.0")}),-1.0]])]});
            var Q41;
            Q41=makeQuery(id+"F13.imprint","IMPRINT",FACE,{"disambiguationData":[TD([[makeQuery(id+"F13.imprint","IMPRINT",EDGE,{"derivedFrom":sQuery(id+"F13.wireOp",EDGE,"E47.33.0.0")}),-1.0]])]});
            var Q42;
            Q42=makeQuery(id+"F13.imprint","IMPRINT",FACE,{"disambiguationData":[TD([[makeQuery(id+"F13.imprint","IMPRINT",EDGE,{"derivedFrom":sQuery(id+"F13.wireOp",EDGE,"E47.34.0.0")}),-1.0]])]});
            var Q43;
            Q43=makeQuery(id+"F13.imprint","IMPRINT",FACE,{"disambiguationData":[TD([[makeQuery(id+"F13.imprint","IMPRINT",EDGE,{"derivedFrom":sQuery(id+"F13.wireOp",EDGE,"E47.35.0.0")}),-1.0]])]});
            var Q44;
            Q44=makeQuery(id+"F13.imprint","IMPRINT",FACE,{"disambiguationData":[TD([[makeQuery(id+"F13.imprint","IMPRINT",EDGE,{"derivedFrom":sQuery(id+"F13.wireOp",EDGE,"E47.36.0.0")}),-1.0]])]});
            var Q45;
            Q45=makeQuery(id+"F13.imprint","IMPRINT",FACE,{"disambiguationData":[TD([[makeQuery(id+"F13.imprint","IMPRINT",EDGE,{"derivedFrom":sQuery(id+"F13.wireOp",EDGE,"E47.38.0.0")}),-1.0]])]});
            var Q46;
            Q46=makeQuery(id+"F13.imprint","IMPRINT",FACE,{"disambiguationData":[TD([[makeQuery(id+"F13.imprint","IMPRINT",EDGE,{"derivedFrom":sQuery(id+"F13.wireOp",EDGE,"E47.39.0.0")}),-1.0]])]});
            var Q47;
            Q47=makeQuery(id+"F13.imprint","IMPRINT",FACE,{"disambiguationData":[TD([[makeQuery(id+"F13.imprint","IMPRINT",EDGE,{"derivedFrom":sQuery(id+"F13.wireOp",EDGE,"E47.42.0.0")}),-1.0]])]});
            var Q48;
            Q48=makeQuery(id+"F13.imprint","IMPRINT",FACE,{"disambiguationData":[TD([[makeQuery(id+"F13.imprint","IMPRINT",EDGE,{"derivedFrom":sQuery(id+"F13.wireOp",EDGE,"E47.43.0.0")}),-1.0]])]});
            var Q49;
            Q49=makeQuery(id+"F13.imprint","IMPRINT",FACE,{"disambiguationData":[TD([[makeQuery(id+"F13.imprint","IMPRINT",EDGE,{"derivedFrom":sQuery(id+"F13.wireOp",EDGE,"E47.45.0.0")}),-1.0]])]});
            var Q50;
            Q50=makeQuery(id+"F13.imprint","IMPRINT",FACE,{"disambiguationData":[TD([[makeQuery(id+"F13.imprint","IMPRINT",EDGE,{"derivedFrom":sQuery(id+"F13.wireOp",EDGE,"E47.46.0.0")}),-1.0]])]});
            var Q51;
            Q51=makeQuery(id+"F13.imprint","IMPRINT",FACE,{"disambiguationData":[TD([[makeQuery(id+"F13.imprint","IMPRINT",EDGE,{"derivedFrom":sQuery(id+"F13.wireOp",EDGE,"E47.48.0.0")}),-1.0]])]});
            var Q52;
            Q52=makeQuery(id+"F13.imprint","IMPRINT",FACE,{"disambiguationData":[TD([[makeQuery(id+"F13.imprint","IMPRINT",EDGE,{"derivedFrom":sQuery(id+"F13.wireOp",EDGE,"E47.49.0.0")}),-1.0]])]});
            var Q53;
            Q53=makeQuery(id+"F13.imprint","IMPRINT",FACE,{"disambiguationData":[TD([[makeQuery(id+"F13.imprint","IMPRINT",EDGE,{"derivedFrom":sQuery(id+"F13.wireOp",EDGE,"E47.51.0.0")}),-1.0]])]});
            var Q54;
            Q54=makeQuery(id+"F13.imprint","IMPRINT",FACE,{"disambiguationData":[TD([[makeQuery(id+"F13.imprint","IMPRINT",EDGE,{"derivedFrom":sQuery(id+"F13.wireOp",EDGE,"E47.53.0.0")}),-1.0]])]});
            var Q55;
            Q55=makeQuery(id+"F13.imprint","IMPRINT",FACE,{"disambiguationData":[TD([[makeQuery(id+"F13.imprint","IMPRINT",EDGE,{"derivedFrom":sQuery(id+"F13.wireOp",EDGE,"E47.54.0.0")}),-1.0]])]});
            var Q56;
            Q56=makeQuery(id+"F13.imprint","IMPRINT",FACE,{"disambiguationData":[TD([[makeQuery(id+"F13.imprint","IMPRINT",EDGE,{"derivedFrom":sQuery(id+"F13.wireOp",EDGE,"E47.56.0.0")}),-1.0]])]});
            var Q57;
            Q57=makeQuery(id+"F13.imprint","IMPRINT",FACE,{"disambiguationData":[TD([[makeQuery(id+"F13.imprint","IMPRINT",EDGE,{"derivedFrom":sQuery(id+"F13.wireOp",EDGE,"E47.57.0.0")}),-1.0]])]});
            var Q58;
            Q58=makeQuery(id+"F13.imprint","IMPRINT",FACE,{"disambiguationData":[TD([[makeQuery(id+"F13.imprint","IMPRINT",EDGE,{"derivedFrom":sQuery(id+"F13.wireOp",EDGE,"E47.58.0.0")}),-1.0]])]});
            var Q59;
            Q59=makeQuery(id+"F13.imprint","IMPRINT",FACE,{"disambiguationData":[TD([[makeQuery(id+"F13.imprint","IMPRINT",EDGE,{"derivedFrom":sQuery(id+"F13.wireOp",EDGE,"E47.59.0.0")}),-1.0]])]});
            extrude(context, id + "F14", {"entities" : qUnion([Q0, Q1, Q2, Q3, Q4, Q5, Q6, Q7, Q8, Q9, Q10, Q11, Q12, Q13, Q14, Q15, Q16, Q17, Q18, Q19, Q20, Q21, Q22, Q23, Q24, Q25, Q26, Q27, Q28, Q29, Q30, Q31, Q32, Q33, Q34, Q35, Q36, Q37, Q38, Q39, Q40, Q41, Q42, Q43, Q44, Q45, Q46, Q47, Q48, Q49, Q50, Q51, Q52, Q53, Q54, Q55, Q56, Q57, Q58, Q59]), "operationType" : NewBodyOperationType.REMOVE, "oppositeDirection" : true, "depth" : 55 * mm});
        }
        {
            var Q0;
            Q0=makeQuery(id+"F2.opExtrude","SWEPT_FACE",FACE,{"disambiguationData":[OSD([sQuery(id+"F0.wireOp",EDGE,"E0")])]});
            var sketch = newSketch(context, id + "F15", { "sketchPlane" : qUnion([Q0])});
            skLineSegment(sketch, "E49", {"start": v(-280, 260) * mm, "end": v(-280, 240) * mm, "construction": true});
            skLineSegment(sketch, "E50", {"start": v(-280, 240) * mm, "end": v(0, 240) * mm});
            skLineSegment(sketch, "E51", {"start": v(0, 240) * mm, "end": v(0, 240) * mm});
            skLineSegment(sketch, "E52", {"start": v(15, 225) * mm, "end": v(15, 225) * mm});
            skLineSegment(sketch, "E53", {"start": v(0, 210) * mm, "end": v(0, 210) * mm});
            skPoint(sketch, "E54.visualSharp", {"position": v(15, 240) * mm});
            skArc(sketch, "E54.filletArc", {"start": v(15, 225) * mm, "mid": v(10.6, 235.6) * mm, "end": v(0, 240) * mm});
            skPoint(sketch, "E55.visualSharp", {"position": v(15, 210) * mm});
            skArc(sketch, "E55.filletArc", {"start": v(0, 210) * mm, "mid": v(10.6, 214.4) * mm, "end": v(15, 225) * mm});
            skLineSegment(sketch, "E56", {"start": v(0, 210) * mm, "end": v(-280, 210) * mm});
            skLineSegment(sketch, "E57", {"start": v(-280, 210) * mm, "end": v(-280, 210) * mm});
            skLineSegment(sketch, "E58", {"start": v(-295, 195) * mm, "end": v(-295, 195) * mm});
            skLineSegment(sketch, "E59", {"start": v(-280, 180) * mm, "end": v(-280, 180) * mm});
            skLineSegment(sketch, "E60", {"start": v(-280, 180) * mm, "end": v(0, 180) * mm});
            skLineSegment(sketch, "E61", {"start": v(0, 180) * mm, "end": v(0, 180) * mm});
            skLineSegment(sketch, "E62", {"start": v(15, 165) * mm, "end": v(15, 165) * mm});
            skLineSegment(sketch, "E63", {"start": v(0, 150) * mm, "end": v(0, 150) * mm});
            skLineSegment(sketch, "E64", {"start": v(0, 150) * mm, "end": v(-280, 150) * mm});
            skLineSegment(sketch, "E65", {"start": v(-280, 150) * mm, "end": v(-280, 150) * mm});
            skLineSegment(sketch, "E66", {"start": v(-295, 135) * mm, "end": v(-295, 135) * mm});
            skLineSegment(sketch, "E67", {"start": v(-280, 120) * mm, "end": v(-280, 120) * mm});
            skLineSegment(sketch, "E68", {"start": v(-280, 120) * mm, "end": v(0, 120) * mm});
            skLineSegment(sketch, "E69", {"start": v(0, 120) * mm, "end": v(0, 120) * mm});
            skLineSegment(sketch, "E70", {"start": v(15, 105) * mm, "end": v(15, 105) * mm});
            skLineSegment(sketch, "E71", {"start": v(0, 90) * mm, "end": v(0, 90) * mm});
            skLineSegment(sketch, "E72", {"start": v(0, 90) * mm, "end": v(-280, 90) * mm});
            skLineSegment(sketch, "E73", {"start": v(-280, 90) * mm, "end": v(-280, 90) * mm});
            skLineSegment(sketch, "E74", {"start": v(-295, 75) * mm, "end": v(-295, 75) * mm});
            skLineSegment(sketch, "E75", {"start": v(-280, 60) * mm, "end": v(-280, 60) * mm});
            skLineSegment(sketch, "E76", {"start": v(-280, 60) * mm, "end": v(0, 60) * mm});
            skLineSegment(sketch, "E77", {"start": v(0, 60) * mm, "end": v(0, 60) * mm});
            skLineSegment(sketch, "E78", {"start": v(15, 45) * mm, "end": v(15, 45) * mm});
            skLineSegment(sketch, "E79", {"start": v(0, 30) * mm, "end": v(0, 30) * mm});
            skLineSegment(sketch, "E80", {"start": v(0, 30) * mm, "end": v(-280, 30) * mm});
            skPoint(sketch, "E81.visualSharp", {"position": v(-295, 210) * mm});
            skArc(sketch, "E81.filletArc", {"start": v(-280, 210) * mm, "mid": v(-290.6, 205.6) * mm, "end": v(-295, 195) * mm});
            skPoint(sketch, "E82.visualSharp", {"position": v(-295, 180) * mm});
            skArc(sketch, "E82.filletArc", {"start": v(-295, 195) * mm, "mid": v(-290.6, 184.4) * mm, "end": v(-280, 180) * mm});
            skPoint(sketch, "E83.visualSharp", {"position": v(15, 180) * mm});
            skArc(sketch, "E83.filletArc", {"start": v(15, 165) * mm, "mid": v(10.6, 175.6) * mm, "end": v(0, 180) * mm});
            skPoint(sketch, "E84.visualSharp", {"position": v(15, 150) * mm});
            skArc(sketch, "E84.filletArc", {"start": v(0, 150) * mm, "mid": v(10.6, 154.4) * mm, "end": v(15, 165) * mm});
            skPoint(sketch, "E85.visualSharp", {"position": v(-295, 150) * mm});
            skArc(sketch, "E85.filletArc", {"start": v(-280, 150) * mm, "mid": v(-290.6, 145.6) * mm, "end": v(-295, 135) * mm});
            skPoint(sketch, "E86.visualSharp", {"position": v(-295, 120) * mm});
            skArc(sketch, "E86.filletArc", {"start": v(-295, 135) * mm, "mid": v(-290.6, 124.4) * mm, "end": v(-280, 120) * mm});
            skPoint(sketch, "E87.visualSharp", {"position": v(15, 120) * mm});
            skArc(sketch, "E87.filletArc", {"start": v(15, 105) * mm, "mid": v(10.6, 115.6) * mm, "end": v(0, 120) * mm});
            skPoint(sketch, "E88.visualSharp", {"position": v(15, 90) * mm});
            skArc(sketch, "E88.filletArc", {"start": v(0, 90) * mm, "mid": v(10.6, 94.4) * mm, "end": v(15, 105) * mm});
            skPoint(sketch, "E89.visualSharp", {"position": v(-295, 90) * mm});
            skArc(sketch, "E89.filletArc", {"start": v(-280, 90) * mm, "mid": v(-290.6, 85.6) * mm, "end": v(-295, 75) * mm});
            skPoint(sketch, "E90.visualSharp", {"position": v(-295, 60) * mm});
            skArc(sketch, "E90.filletArc", {"start": v(-295, 75) * mm, "mid": v(-290.6, 64.4) * mm, "end": v(-280, 60) * mm});
            skPoint(sketch, "E91.visualSharp", {"position": v(15, 60) * mm});
            skArc(sketch, "E91.filletArc", {"start": v(15, 45) * mm, "mid": v(10.6, 55.6) * mm, "end": v(0, 60) * mm});
            skPoint(sketch, "E92.visualSharp", {"position": v(15, 30) * mm});
            skArc(sketch, "E92.filletArc", {"start": v(0, 30) * mm, "mid": v(10.6, 34.4) * mm, "end": v(15, 45) * mm});
            skSolve(sketch);
        }
        {
            var Q0;
            Q0=makeQuery(id+"F10.imprint","IMPRINT",FACE,{"disambiguationData":[TD([[makeQuery(id+"F10.imprint","IMPRINT",EDGE,{"derivedFrom":sQuery(id+"F10.wireOp",EDGE,"E31")}),1.0]])]});
            var Q1;
            Q1=sQuery(id+"F15.wireOp",EDGE,"E50");
            var Q2;
            Q2=sQuery(id+"F15.wireOp",EDGE,"E54.filletArc");
            var Q3;
            Q3=sQuery(id+"F15.wireOp",EDGE,"E55.filletArc");
            var Q4;
            Q4=sQuery(id+"F15.wireOp",EDGE,"E56");
            var Q5;
            Q5=sQuery(id+"F15.wireOp",EDGE,"E81.filletArc");
            var Q6;
            Q6=sQuery(id+"F15.wireOp",EDGE,"E82.filletArc");
            var Q7;
            Q7=sQuery(id+"F15.wireOp",EDGE,"E60");
            var Q8;
            Q8=sQuery(id+"F15.wireOp",EDGE,"E83.filletArc");
            var Q9;
            Q9=sQuery(id+"F15.wireOp",EDGE,"E84.filletArc");
            var Q10;
            Q10=sQuery(id+"F15.wireOp",EDGE,"E64");
            var Q11;
            Q11=sQuery(id+"F15.wireOp",EDGE,"E85.filletArc");
            var Q12;
            Q12=sQuery(id+"F15.wireOp",EDGE,"E86.filletArc");
            var Q13;
            Q13=sQuery(id+"F15.wireOp",EDGE,"E68");
            var Q14;
            Q14=sQuery(id+"F15.wireOp",EDGE,"E87.filletArc");
            var Q15;
            Q15=sQuery(id+"F15.wireOp",EDGE,"E88.filletArc");
            var Q16;
            Q16=sQuery(id+"F15.wireOp",EDGE,"E72");
            var Q17;
            Q17=sQuery(id+"F15.wireOp",EDGE,"E89.filletArc");
            var Q18;
            Q18=sQuery(id+"F15.wireOp",EDGE,"E90.filletArc");
            var Q19;
            Q19=sQuery(id+"F15.wireOp",EDGE,"E76");
            var Q20;
            Q20=sQuery(id+"F15.wireOp",EDGE,"E91.filletArc");
            var Q21;
            Q21=sQuery(id+"F15.wireOp",EDGE,"E92.filletArc");
            var Q22;
            Q22=sQuery(id+"F15.wireOp",EDGE,"E80");
            sweep(context, id + "F16", {"operationType" : NewBodyOperationType.ADD, "profiles" : qUnion([Q0]), "path" : qUnion([Q1, Q2, Q3, Q4, Q5, Q6, Q7, Q8, Q9, Q10, Q11, Q12, Q13, Q14, Q15, Q16, Q17, Q18, Q19, Q20, Q21, Q22])});
        }
    });
